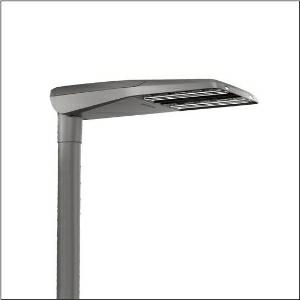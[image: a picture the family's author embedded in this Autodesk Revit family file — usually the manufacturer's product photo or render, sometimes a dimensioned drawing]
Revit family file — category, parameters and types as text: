
# Revit family: streetlight_sl_11_iq_midi___st1_0ab_5xc3n51f08le_f358
name_source: partatom
category: Lighting Fixtures
units: mm (PartAtom-declared; Revit-internal decimal feet)

## family parameters
Cut with Voids When Loaded = No
Host = Face
Light Source = No
Part Type = Normal
Room Calculation Point = No
Round Connector Dimension = Use Diameter
Shared = No

## types (1)
- --- (1 x LED, 7760 lm, 60.4 W, 3000K)
    Apparent Load = 60 VA
    CIE Flux Codes = 29 63 95 100 100
    Color Rendering = 70
    Color Temperature = 3000K
    Default Elevation = 1800 mm
    Description = Streetlight SL 11 iQ midi, mast luminaire, primary light control with 3 zone facetted reflector, of plastic, silver coated, highly specular, primary optical cover: cover, of PMMA, transparent, light distribution: ST1.0aB, light emission: direct distribution, primary light characteristic: asymmetric, installation type: post-top, side-entry, lamps: LED, High Power LED, rated values: 7.760lm | 60,4W | 128,5lm/W (begin service life); end service life: 7.760lm | 62,5W; at 50% lumin. flux: 3.880lm | 29,6W | 131,1lm/W, colour temperature: 3000K, colour rendering: CRI > 70, light colour: 730, light setting 1 begin service life: 100% | 7.760lm | 60,4W | 128,5lm/W | 3.000K, light setting 1 end service life: 62,5W, further light settings possible, control: optimised constant luminous flux control (CLO 2.0), Street-Remote, Desk-Remote (wireless, voltage-free reading and setting of iQ features in the workshop via application-optimized NFC function/RFID function), Light-Fading, Smart-Wire, Night-Set, Lumen-Switch, Temp-Guard, Auto-Match, with cable H07RN-F 5x 1.5mm², mains connection: 230..240V, AC, 50/60Hz, connection cable pre-assembled, cable length: 8,5m, luminaire housing, of diecast aluminium, powder-coated, Siteco® metallic grey (DB 702S), please order mast flange separately, inclination adjustable without tools: 0°, 5°, 10°, 15° (post-top) | 0°, -5°, -10°, -15° (side-entry), sealing non-destructively replaceable, multi-level sealing system, length: 780mm, width: 376mm, height: 118mm, mast flange for spigot size: 42mm (side-entry): 5XC10008XM4, 60/48mm (side-entry/post-top): 5XC10108XM2, 76/60mm (side-entry/post-top): 5XC10108XM1, equipment: standard, protection rating (complete): IP66, insulation class (complete): insulation class II (safety insulation), certification: CE, ENEC, ENEC+, VDE, impact resistance: IK10, permissible operating ambient temperature for outdoor applications: -25..+50°C, standard-compliant lighting for roads and squares, Environmental Product Declaration (EPD) tested and certified by an independent institute, packaging unit: 1 piece

Light Distribution: ST1.0aB
    Height = 118 mm
    Lamp = 1 x LED
    Lamp Light Flux = 7760 lm
    Lamp Power = 60.4 W
    Lamp count = 1
    Length = 780 mm
    Luminous efficacy = 128 lm/W
    Manufacturer = Siteco
    ModVariant = No
    Model = 5XC3N51F08LE
    Number of Poles = 1
    OnlyDefault = Yes
    Power Factor = 1
    Product Name = Streetlight SL 11 iQ midi | ST1.0aB
    Product group = mast luminaire | pylon top
    ProductGroupID = 6100
    Protection Class = Protection class II
    Protection Degree = IP 66
    RLX_Detail_Level = 1
    RLX_Emergency_Light_Flux = 0 lm
    RLX_Emergency_Type = 0
    RLX_Emergency_Type_DB = No
    RlxData = <blob elided: 70509 chars, md5=14d19381>
    Socket = socket
    Standby Power = 0 W
    System Light Flux = 7760 lm
    System Power = 60 W
    Type Comments = factory setting: luminous flux: 100 % | dim-lin: 254 | 520 mA
    Type Image = l_1005960.jpg
    URL = http://relux.com
    VarID = @adj_109485
    Voltage = 0 V
    Weight = 0.00 kg
    Width = 376 mm

## geometry (parser evidence)
native form markers: Blend x4, Sweep x11
no freeform markers — native parametric forms only
